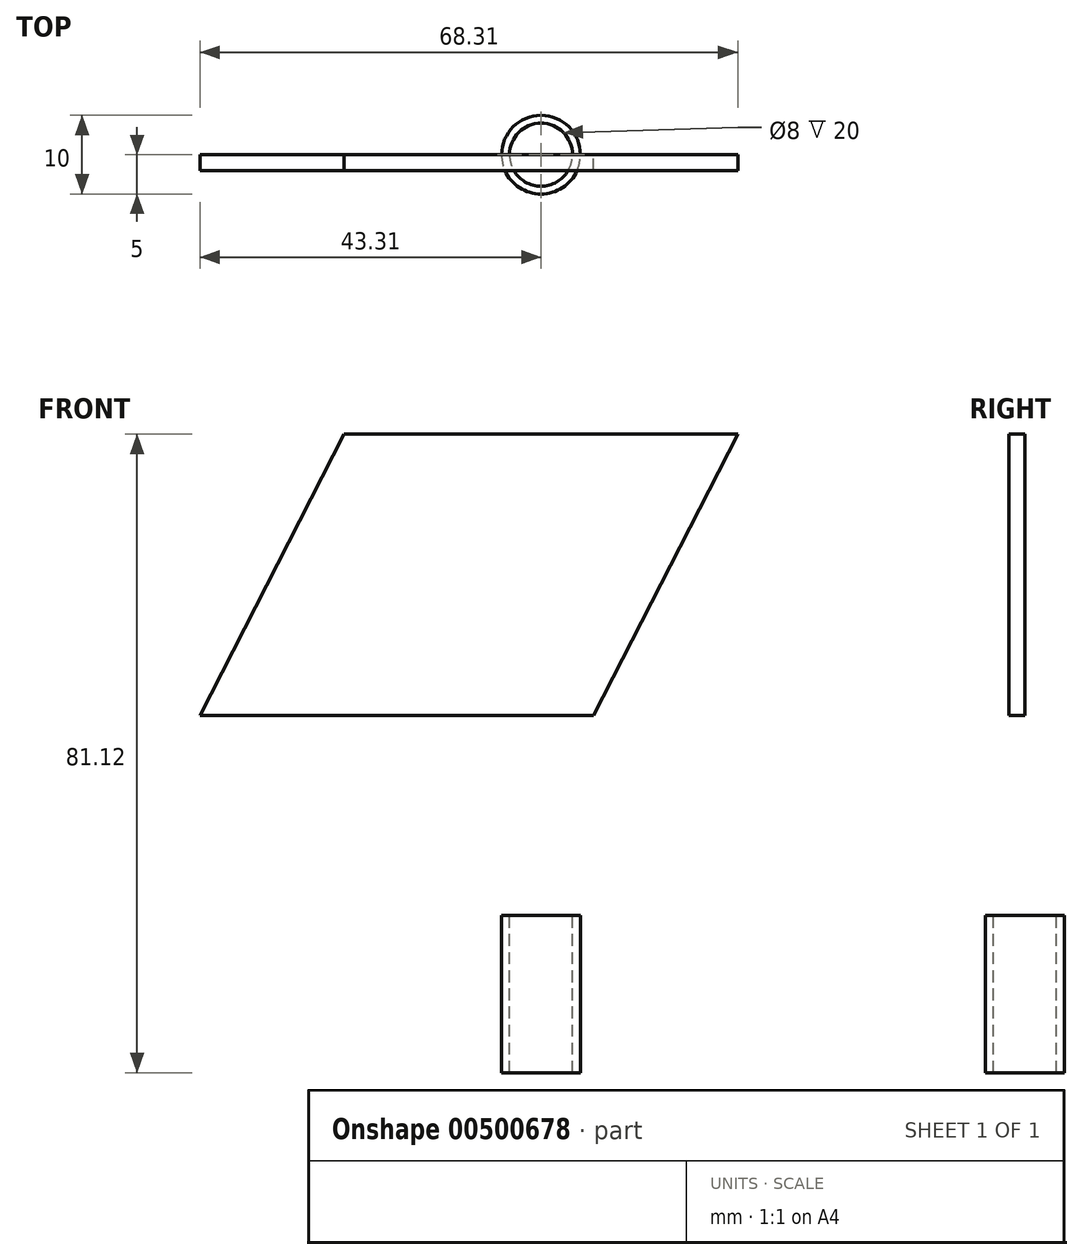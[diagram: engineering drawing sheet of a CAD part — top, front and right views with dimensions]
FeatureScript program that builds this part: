
annotation { "Feature Type Name" : "Feature", "Feature Type Description" : "" }
export const myFeature = defineFeature(function(context is Context, id is Id, definition is map)
    precondition{}
    {
        {
            var Q0;
            Q0=qCreatedBy(makeId("Front.planeOp"),FACE);
            var sketch = newSketch(context, id + "F0", { "sketchPlane" : qUnion([Q0])});
            skLineSegment(sketch, "E0", {"start": v(0, 35.72) * mm, "end": v(-25, 35.72) * mm});
            skLineSegment(sketch, "E1", {"start": v(0, 35.72) * mm, "end": v(25, 35.72) * mm});
            skLineSegment(sketch, "E2", {"start": v(-25, 35.72) * mm, "end": v(-43.31, 0) * mm});
            skLineSegment(sketch, "E3", {"start": v(-43.31, 0) * mm, "end": v(6.69, 0) * mm});
            skLineSegment(sketch, "E4", {"start": v(25, 35.72) * mm, "end": v(6.69, 0) * mm});
            skSolve(sketch);
        }
        {
            var Q0;
            Q0=makeQuery(id+"F0.imprint","IMPRINT",FACE,{"disambiguationData":[TD([[makeQuery(id+"F0.imprint","IMPRINT",EDGE,{"derivedFrom":sQuery(id+"F0.wireOp",EDGE,"E0")}),1.0]])]});
            extrude(context, id + "F1", {"entities" : qUnion([Q0]), "depth" : 2 * mm, "offsetDistance" : 25.4 * mm});
        }
        {
            var Q0;
            Q0=qCreatedBy(makeId("Top.planeOp"),FACE);
            cPlane(context, id + "F2", {"entities" : qUnion([Q0]), "cplaneType" : CPlaneType.OFFSET, "offset" : 25.4 * mm, "oppositeDirection" : true, "width" : 152.4 * mm, "height" : 152.4 * mm});
        }
        {
            var Q0;
            Q0=qCreatedBy(id+"F2.planeOp",FACE);
            var sketch = newSketch(context, id + "F3", { "sketchPlane" : qUnion([Q0])});
            skCircle(sketch, "E5", {"center": v(0, 0) * mm, "radius": 5 * mm});
            skCircle(sketch, "E6", {"center": v(0, 0) * mm, "radius": 4 * mm});
            skSolve(sketch);
        }
        {
            var Q0;
            Q0 = qSketchRegion(id + "F3", true);
            extrude(context, id + "F4", {"entities" : qUnion([Q0]), "oppositeDirection" : true, "depth" : 20 * mm, "offsetDistance" : 25.4 * mm});
        }
    });
